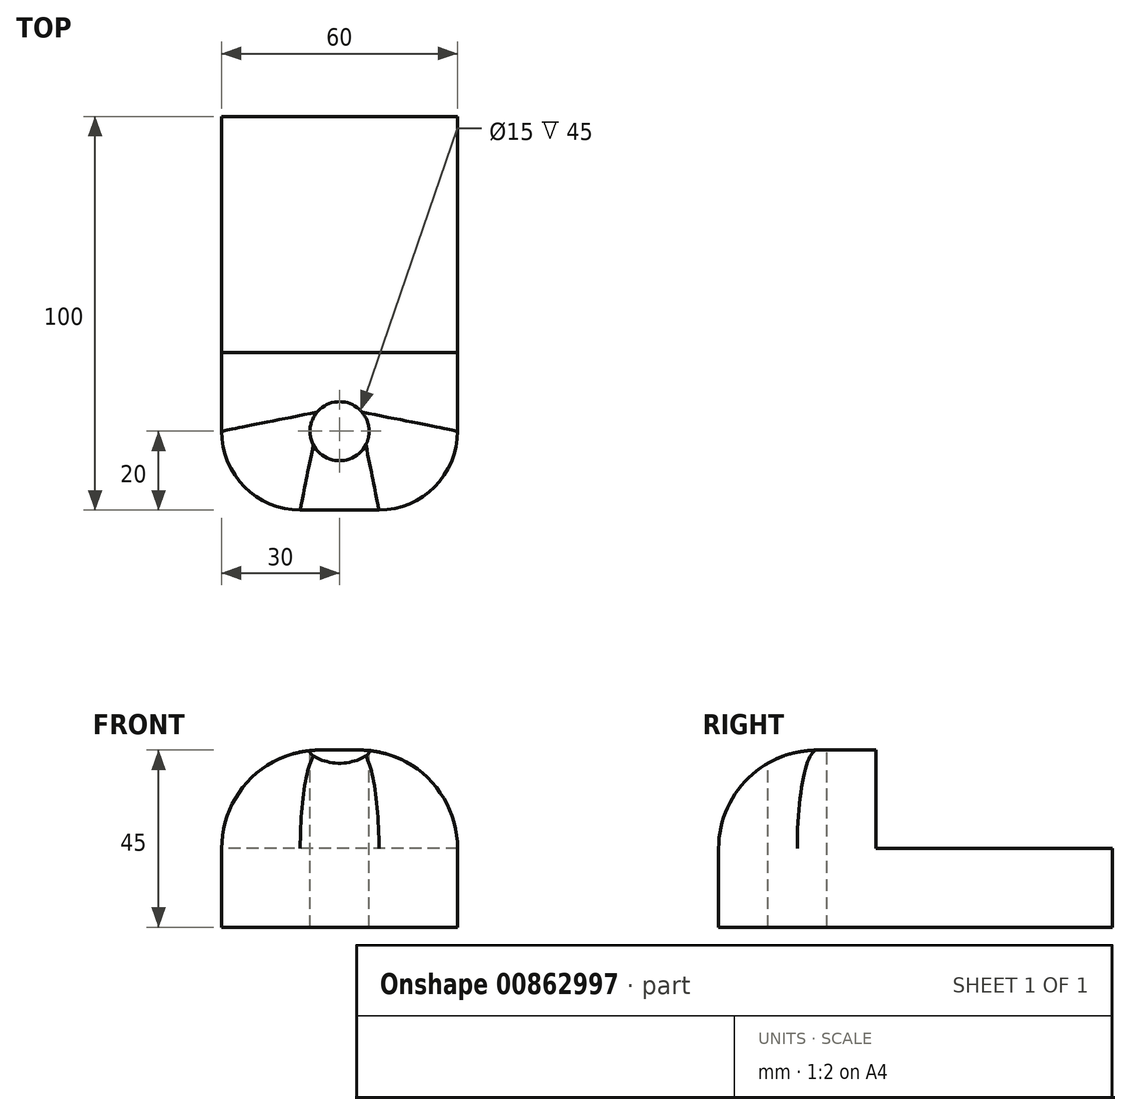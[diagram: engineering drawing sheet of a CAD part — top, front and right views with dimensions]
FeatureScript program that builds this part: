
annotation { "Feature Type Name" : "Feature", "Feature Type Description" : "" }
export const myFeature = defineFeature(function(context is Context, id is Id, definition is map)
    precondition{}
    {
        {
            var Q0;
            Q0=qCreatedBy(makeId("Top.planeOp"),FACE);
            var sketch = newSketch(context, id + "F0", { "sketchPlane" : qUnion([Q0])});
            skLineSegment(sketch, "E0.bottom", {"start": v(30, 50) * mm, "end": v(-30, 50) * mm});
            skLineSegment(sketch, "E0.top", {"start": v(10, -50) * mm, "end": v(-10, -50) * mm});
            skLineSegment(sketch, "E0.left", {"start": v(30, 50) * mm, "end": v(30, -30) * mm});
            skLineSegment(sketch, "E0.right", {"start": v(-30, 50) * mm, "end": v(-30, -30) * mm});
            skPoint(sketch, "E0.middle", {"position": v(0, 0) * mm});
            skPoint(sketch, "E1.visualSharp", {"position": v(-30, -50) * mm});
            skArc(sketch, "E1.filletArc", {"start": v(-30, -30) * mm, "mid": v(-24.14, -44.14) * mm, "end": v(-10, -50) * mm});
            skPoint(sketch, "E2.visualSharp", {"position": v(30, -50) * mm});
            skArc(sketch, "E2.filletArc", {"start": v(10, -50) * mm, "mid": v(24.14, -44.14) * mm, "end": v(30, -30) * mm});
            skSolve(sketch);
        }
        {
            var Q0;
            Q0=makeQuery(id+"F0.imprint","IMPRINT",FACE,{"disambiguationData":[TD([[makeQuery(id+"F0.imprint","IMPRINT",EDGE,{"derivedFrom":sQuery(id+"F0.wireOp",EDGE,"E0.bottom")}),1.0]])]});
            extrude(context, id + "F1", {"entities" : qUnion([Q0]), "depth" : 45 * mm, "offsetDistance" : 25 * mm});
        }
        {
            var Q0;
            Q0=makeQuery(id+"F1.opExtrude","CAP_FACE",FACE,{"disambiguationData":[OSD([sQuery(id+"F0.wireOp",EDGE,"E0.bottom"),sQuery(id+"F0.wireOp",EDGE,"E0.top"),sQuery(id+"F0.wireOp",EDGE,"E0.left"),sQuery(id+"F0.wireOp",EDGE,"E0.right"),sQuery(id+"F0.wireOp",EDGE,"E1.filletArc"),sQuery(id+"F0.wireOp",EDGE,"E2.filletArc")])],"isStart":false});
            var sketch = newSketch(context, id + "F2", { "sketchPlane" : qUnion([Q0])});
            skLineSegment(sketch, "E3", {"start": v(-30, -10) * mm, "end": v(30, -10) * mm});
            skSolve(sketch);
        }
        {
            var Q0;
            {var subQ0=sQuery(id+"F2.wireOp",EDGE,"E3");Q0=makeQuery(id+"F2.imprint","IMPRINT",FACE,{"disambiguationData":[TD([[makeQuery(id+"F2.imprint","IMPRINT",EDGE,{"derivedFrom":subQ0}),1.0]])]});}
            extrude(context, id + "F3", {"entities" : qUnion([Q0]), "operationType" : NewBodyOperationType.REMOVE, "oppositeDirection" : true, "depth" : 25 * mm, "offsetDistance" : 25 * mm});
        }
        {
            var Q0;
            Q0=makeQuery(id+"F1.opExtrude","CAP_FACE",FACE,{"disambiguationData":[OSD([sQuery(id+"F0.wireOp",EDGE,"E0.bottom"),sQuery(id+"F0.wireOp",EDGE,"E0.top"),sQuery(id+"F0.wireOp",EDGE,"E0.left"),sQuery(id+"F0.wireOp",EDGE,"E0.right"),sQuery(id+"F0.wireOp",EDGE,"E1.filletArc"),sQuery(id+"F0.wireOp",EDGE,"E2.filletArc")])],"isStart":false});
            var sketch = newSketch(context, id + "F4", { "sketchPlane" : qUnion([Q0])});
            skCircle(sketch, "E4", {"center": v(0, -30) * mm, "radius": 7.5 * mm});
            skSolve(sketch);
        }
        {
            var Q0;
            Q0=makeQuery(id+"F4.imprint","IMPRINT",FACE,{"disambiguationData":[TD([[makeQuery(id+"F4.imprint","IMPRINT",EDGE,{"derivedFrom":sQuery(id+"F4.wireOp",EDGE,"E4")}),1.0]])]});
            extrude(context, id + "F5", {"entities" : qUnion([Q0]), "operationType" : NewBodyOperationType.REMOVE, "endBound" : BoundingType.THROUGH_ALL, "oppositeDirection" : true, "depth" : 25 * mm, "offsetDistance" : 25 * mm});
        }
        {
            var Q0;
            Q0=makeQuery(id+"F1.opExtrude","CAP_EDGE",EDGE,{"disambiguationData":[OSD([sQuery(id+"F0.wireOp",EDGE,"E0.right")])],"isStart":false});
            fillet(context, id + "F6", {"entities" : qUnion([Q0]), "radius" : 25 * mm, "tangentPropagation" : true, "allowEdgeOverflow" : false});
        }
    });
